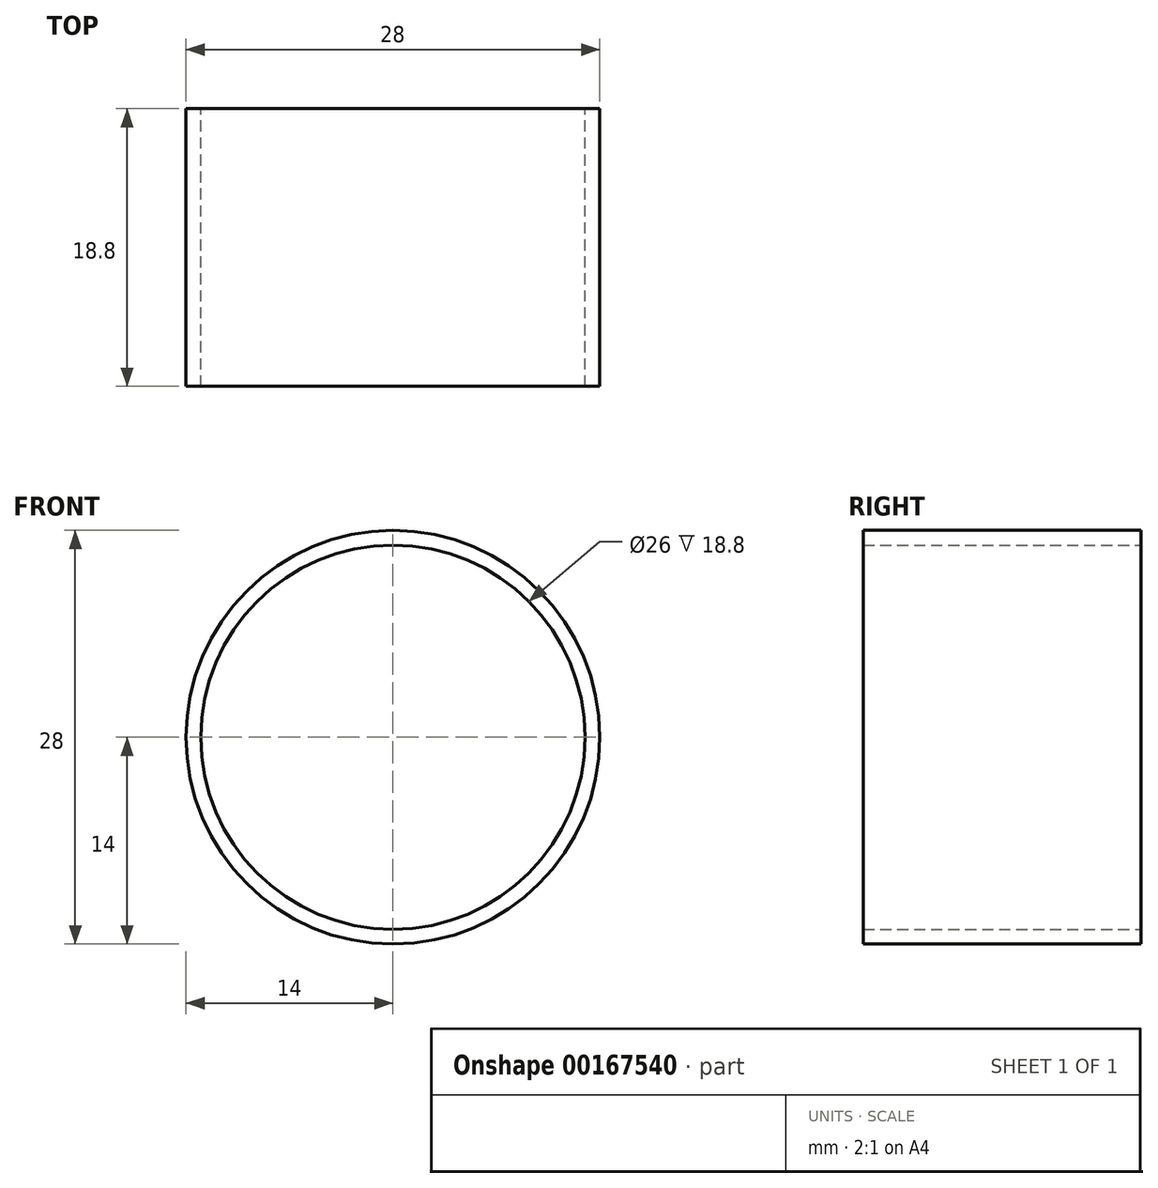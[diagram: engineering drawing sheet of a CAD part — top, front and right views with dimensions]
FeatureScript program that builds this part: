
annotation { "Feature Type Name" : "Feature", "Feature Type Description" : "" }
export const myFeature = defineFeature(function(context is Context, id is Id, definition is map)
    precondition{}
    {
        {
            var Q0;
            Q0=qCreatedBy(makeId("Front.planeOp"),FACE);
            var sketch = newSketch(context, id + "F0", { "sketchPlane" : qUnion([Q0])});
            skCircle(sketch, "E0", {"center": v(0, 0) * mm, "radius": 14 * mm});
            skCircle(sketch, "E1", {"center": v(0, 0) * mm, "radius": 13 * mm});
            skSolve(sketch);
        }
        {
            var Q0;
            Q0=qSketchRegion(id+"F0",true);
            extrude(context, id + "F1", {"entities" : qUnion([Q0]), "depth" : 18.8 * mm, "symmetric" : true});
        }
    });
